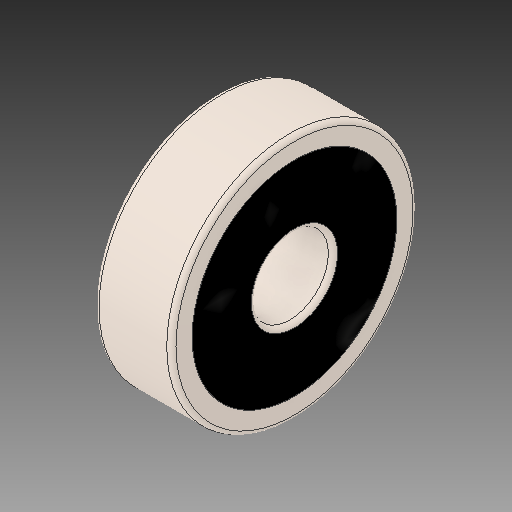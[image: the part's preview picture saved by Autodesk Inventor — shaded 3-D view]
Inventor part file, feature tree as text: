
AUTODESK INVENTOR PART (.ipt)
format: ipt  version: 2017 (Build 210142000, 142)  size: 2,296,320 bytes
history: imported  units: mm
features: other x22, sketch x2, imported_body x1
ambient origin geometry x8: Origin, YZ Plane, XZ Plane, XY Plane, X Axis, Y Axis, Z Axis, Center Point
bodies: Solid1 (imported_parasolid), Solid2 (imported_parasolid), Solid3 (imported_parasolid), Solid4 (imported_parasolid), Solid5 (imported_parasolid), Solid6 (imported_parasolid), Solid7 (imported_parasolid), Solid8 (imported_parasolid), Solid9 (imported_parasolid), Solid10 (imported_parasolid), Solid11 (imported_parasolid), Solid12 (imported_parasolid), Solid13 (imported_parasolid), Solid14 (imported_parasolid), Solid15 (imported_parasolid), Solid16 (imported_parasolid), Solid17 (imported_parasolid), Solid18 (imported_parasolid), Solid19 (imported_parasolid), Solid20 (imported_parasolid)
feature tree (25):
  other  "SKF 625_CPY.ipt"
  other  "Solid1::SKF 625_CPY.ipt"
  other  "Solid2::SKF 625_CPY.ipt"
  other  "Solid3::SKF 625_CPY.ipt"
  other  "Solid4::SKF 625_CPY.ipt"
  other  "Solid5::SKF 625_CPY.ipt"
  other  "Solid6::SKF 625_CPY.ipt"
  other  "Solid7::SKF 625_CPY.ipt"
  other  "Solid8::SKF 625_CPY.ipt"
  other  "Solid9::SKF 625_CPY.ipt"
  other  "Solid10::SKF 625_CPY.ipt"
  other  "Solid11::SKF 625_CPY.ipt"
  other  "Solid12::SKF 625_CPY.ipt"
  other  "Solid13::SKF 625_CPY.ipt"
  other  "Solid14::SKF 625_CPY.ipt"
  other  "Solid15::SKF 625_CPY.ipt"
  other  "Solid16::SKF 625_CPY.ipt"
  other  "Solid17::SKF 625_CPY.ipt"
  other  "Solid18::SKF 625_CPY.ipt"
  other  "Solid19::SKF 625_CPY.ipt"
  other  "Solid20::SKF 625_CPY.ipt"
  other  "TaggingFeature1"
  sketch  "Sketch1"  dims[d0=10.0mm]
  sketch  "Sketch2"
  imported_body  NMx_Import_Brep_tag  [imported B-rep: ~49 faces, bbox_mm=None]
